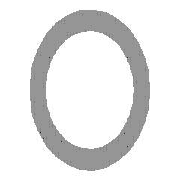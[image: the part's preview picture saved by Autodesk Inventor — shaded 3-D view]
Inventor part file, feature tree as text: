
AUTODESK INVENTOR PART (.ipt)
format: ipt  version: 2025 (Build 290162010, 162A)  size: 123,904 bytes
history: native  units: mm (DEFAULTED — no unit token found)
features: other x3, sketch x1, plane x1
ambient origin geometry x8: Origin, YZ Plane, XZ Plane, XY Plane, X Axis, Y Axis, Z Axis, Center Point
bodies: Solid1 (feature_tree), Body (feature_tree)
feature tree (5):
  other  "Driven Length"
  other  "Start plane"
  other  "End plane"
  sketch  "Sketch3"  dims[d0=168.3mm d1=2.0mm d2=650.0mm d3=0.0mm d4=-0.0mm d5=650.0mm d6=90.0deg d7=650.0mm]
  plane  "Work Plane3"
